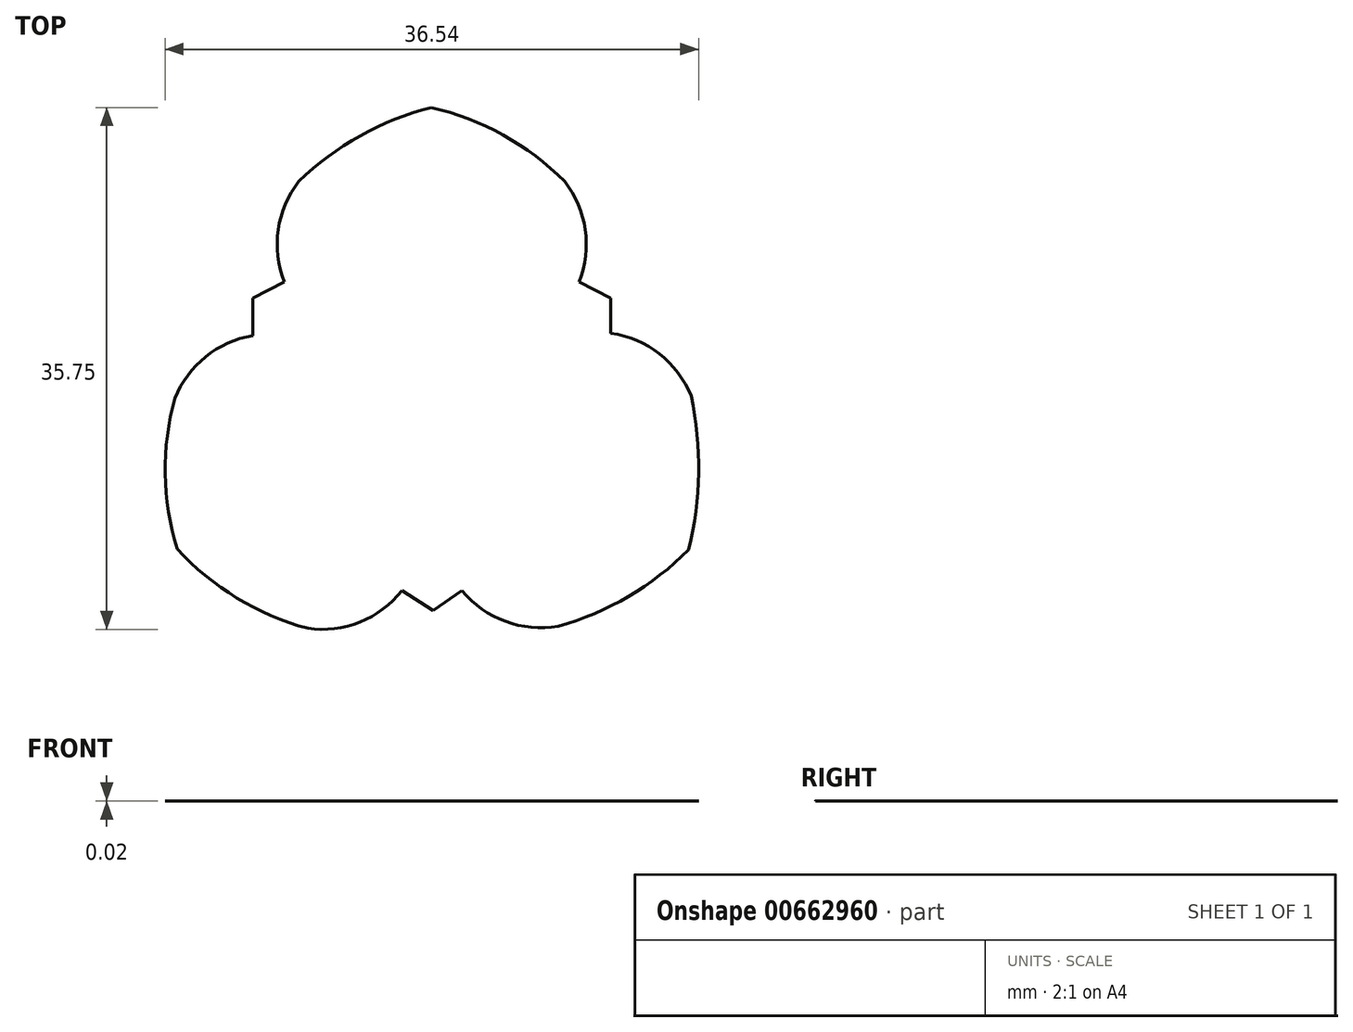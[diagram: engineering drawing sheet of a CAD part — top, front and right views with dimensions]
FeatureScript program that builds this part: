
annotation { "Feature Type Name" : "Feature", "Feature Type Description" : "" }
export const myFeature = defineFeature(function(context is Context, id is Id, definition is map)
    precondition{}
    {
        {
            var Q0;
            Q0=qCreatedBy(makeId("Top.planeOp"),FACE);
            var sketch = newSketch(context, id + "F0", { "sketchPlane" : qUnion([Q0])});
            skPoint(sketch, "E0.center", {"position": v(0, 0) * mm});
            skArc(sketch, "E1", {"start": v(-9.2, 15.13) * mm, "mid": v(-10.62, 11.82) * mm, "end": v(-10.2, 8.25) * mm});
            skLineSegment(sketch, "E2", {"start": v(-10.2, 8.25) * mm, "end": v(-12.37, 7.15) * mm});
            skLineSegment(sketch, "E3", {"start": v(-12.37, 7.15) * mm, "end": v(-12.37, 4.64) * mm});
            skLineSegment(sketch, "E4.MirrorCS", {"start": v(12.16, 7.15) * mm, "end": v(12.16, 4.64) * mm});
            skLineSegment(sketch, "E5.MirrorCS", {"start": v(10, 8.25) * mm, "end": v(12.16, 7.15) * mm});
            skArc(sketch, "E6.MirrorCS", {"start": v(9, 15.13) * mm, "mid": v(10.4, 11.82) * mm, "end": v(10, 8.25) * mm});
            skArc(sketch, "E7", {"start": v(17.66, 0.43) * mm, "mid": v(15.48, 3.32) * mm, "end": v(12.16, 4.74) * mm});
            skArc(sketch, "E8.MirrorCS", {"start": v(8.56, -15.34) * mm, "mid": v(4.94, -15) * mm, "end": v(1.97, -12.9) * mm});
            skLineSegment(sketch, "E9", {"start": v(1.97, -12.9) * mm, "end": v(0, -14.26) * mm});
            skLineSegment(sketch, "E10", {"start": v(0, -14.26) * mm, "end": v(-2.14, -12.9) * mm});
            skArc(sketch, "E11", {"start": v(-8.6, -15.48) * mm, "mid": v(-5.03, -15.05) * mm, "end": v(-2.14, -12.9) * mm});
            skArc(sketch, "E12.MirrorCS", {"start": v(-17.7, 0.28) * mm, "mid": v(-15.6, 3.12) * mm, "end": v(-12.37, 4.57) * mm});
            skLineSegment(sketch, "E13", {"start": v(-12.37, 4.64) * mm, "end": v(-12.37, 4.57) * mm});
            skArc(sketch, "E14", {"start": v(-0.14, 20.2) * mm, "mid": v(-5, 18.26) * mm, "end": v(-9.2, 15.13) * mm});
            skArc(sketch, "E15", {"start": v(9, 15.13) * mm, "mid": v(4.78, 18.3) * mm, "end": v(-0.14, 20.2) * mm});
            skArc(sketch, "E16", {"start": v(17.49, -10.1) * mm, "mid": v(18.17, -4.84) * mm, "end": v(17.66, 0.43) * mm});
            skArc(sketch, "E17", {"start": v(8.56, -15.34) * mm, "mid": v(13.37, -13.3) * mm, "end": v(17.49, -10.1) * mm});
            skArc(sketch, "E18", {"start": v(-17.7, 0.28) * mm, "mid": v(-18.36, -4.89) * mm, "end": v(-17.55, -10.04) * mm});
            skArc(sketch, "E19", {"start": v(-17.55, -10.04) * mm, "mid": v(-13.46, -13.4) * mm, "end": v(-8.6, -15.48) * mm});
            skSolve(sketch);
        }
        {
            var Q0;
            Q0=makeQuery(id+"F0.imprint","IMPRINT",FACE,{"disambiguationData":[TD([[makeQuery(id+"F0.imprint","IMPRINT",EDGE,{"derivedFrom":sQuery(id+"F0.wireOp",EDGE,"E1")}),1.0]])]});
            extrude(context, id + "F1", {"entities" : qUnion([Q0]), "depth" : 7 / 406.4 * mm, "offsetDistance" : 25.4 * mm});
        }
    });
